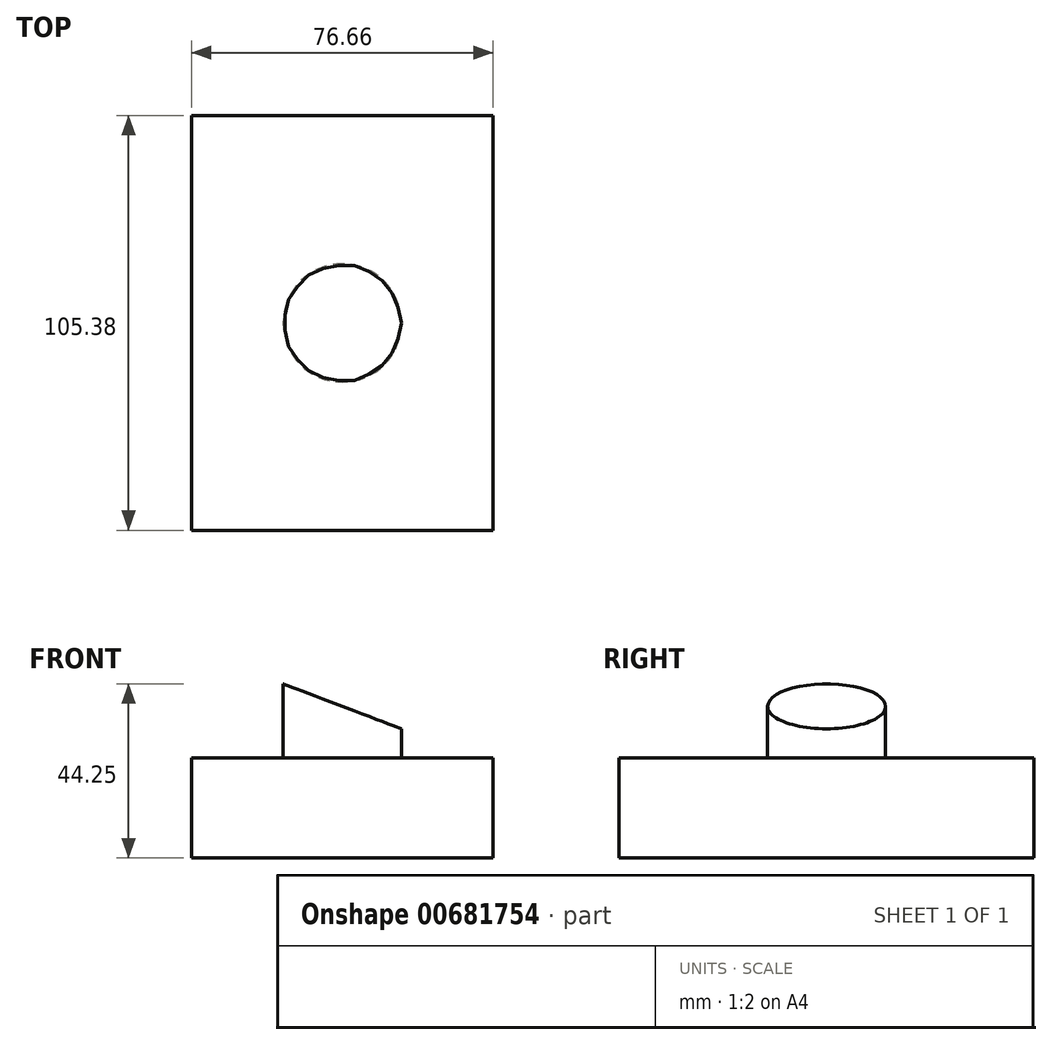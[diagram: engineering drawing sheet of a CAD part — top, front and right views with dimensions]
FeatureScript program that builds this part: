
annotation { "Feature Type Name" : "Feature", "Feature Type Description" : "" }
export const myFeature = defineFeature(function(context is Context, id is Id, definition is map)
    precondition{}
    {
        {
            var Q0;
            Q0=qCreatedBy(makeId("Top.planeOp"),FACE);
            var sketch = newSketch(context, id + "F0", { "sketchPlane" : qUnion([Q0])});
            skLineSegment(sketch, "E0.bottom", {"start": v(38.33, -52.69) * mm, "end": v(-38.33, -52.69) * mm});
            skLineSegment(sketch, "E0.top", {"start": v(38.33, 52.69) * mm, "end": v(-38.33, 52.69) * mm});
            skLineSegment(sketch, "E0.left", {"start": v(38.33, -52.69) * mm, "end": v(38.33, 52.69) * mm});
            skLineSegment(sketch, "E0.right", {"start": v(-38.33, -52.69) * mm, "end": v(-38.33, 52.69) * mm});
            skPoint(sketch, "E0.middle", {"position": v(0, 0) * mm});
            skSolve(sketch);
        }
        {
            var Q0;
            Q0=makeQuery(id+"F0.imprint","IMPRINT",FACE,{"disambiguationData":[TD([[makeQuery(id+"F0.imprint","IMPRINT",EDGE,{"derivedFrom":sQuery(id+"F0.wireOp",EDGE,"E0.bottom")}),-1.0]])]});
            extrude(context, id + "F1", {"entities" : qUnion([Q0]), "depth" : 25.4 * mm, "offsetDistance" : 25.4 * mm});
        }
        {
            var Q0;
            Q0=makeQuery(id+"F1.opExtrude","CAP_FACE",FACE,{"disambiguationData":[OSD([sQuery(id+"F0.wireOp",EDGE,"E0.bottom"),sQuery(id+"F0.wireOp",EDGE,"E0.top"),sQuery(id+"F0.wireOp",EDGE,"E0.left"),sQuery(id+"F0.wireOp",EDGE,"E0.right")])],"isStart":false});
            var sketch = newSketch(context, id + "F2", { "sketchPlane" : qUnion([Q0])});
            skCircle(sketch, "E1", {"center": v(0, 0) * mm, "radius": 15 * mm});
            skSolve(sketch);
        }
        {
            var Q0;
            Q0 = qSketchRegion(id + "F2", true);
            extrude(context, id + "F3", {"entities" : qUnion([Q0]), "operationType" : NewBodyOperationType.ADD, "depth" : 19.05 * mm, "offsetDistance" : 25.4 * mm});
        }
        {
            var Q0;
            Q0=qCreatedBy(makeId("Front.planeOp"),FACE);
            var sketch = newSketch(context, id + "F4", { "sketchPlane" : qUnion([Q0])});
            skLineSegment(sketch, "E2", {"start": v(-18.56, 45.6) * mm, "end": v(23.6, 29.56) * mm});
            skLineSegment(sketch, "E3", {"start": v(23.6, 29.56) * mm, "end": v(23.6, 54.93) * mm});
            skLineSegment(sketch, "E4", {"start": v(23.6, 54.93) * mm, "end": v(-18.56, 45.6) * mm});
            skSolve(sketch);
        }
        {
            var Q0;
            Q0=makeQuery(id+"F4.imprint","IMPRINT",FACE,{"disambiguationData":[TD([[makeQuery(id+"F4.imprint","IMPRINT",EDGE,{"derivedFrom":sQuery(id+"F4.wireOp",EDGE,"E2")}),1.0]])]});
            extrude(context, id + "F5", {"entities" : qUnion([Q0]), "operationType" : NewBodyOperationType.REMOVE, "depth" : 25.4 * mm, "offsetDistance" : 25.4 * mm, "hasSecondDirection" : true, "secondDirectionOppositeDirection" : true, "secondDirectionDepth" : 25.4 * mm});
        }
    });
